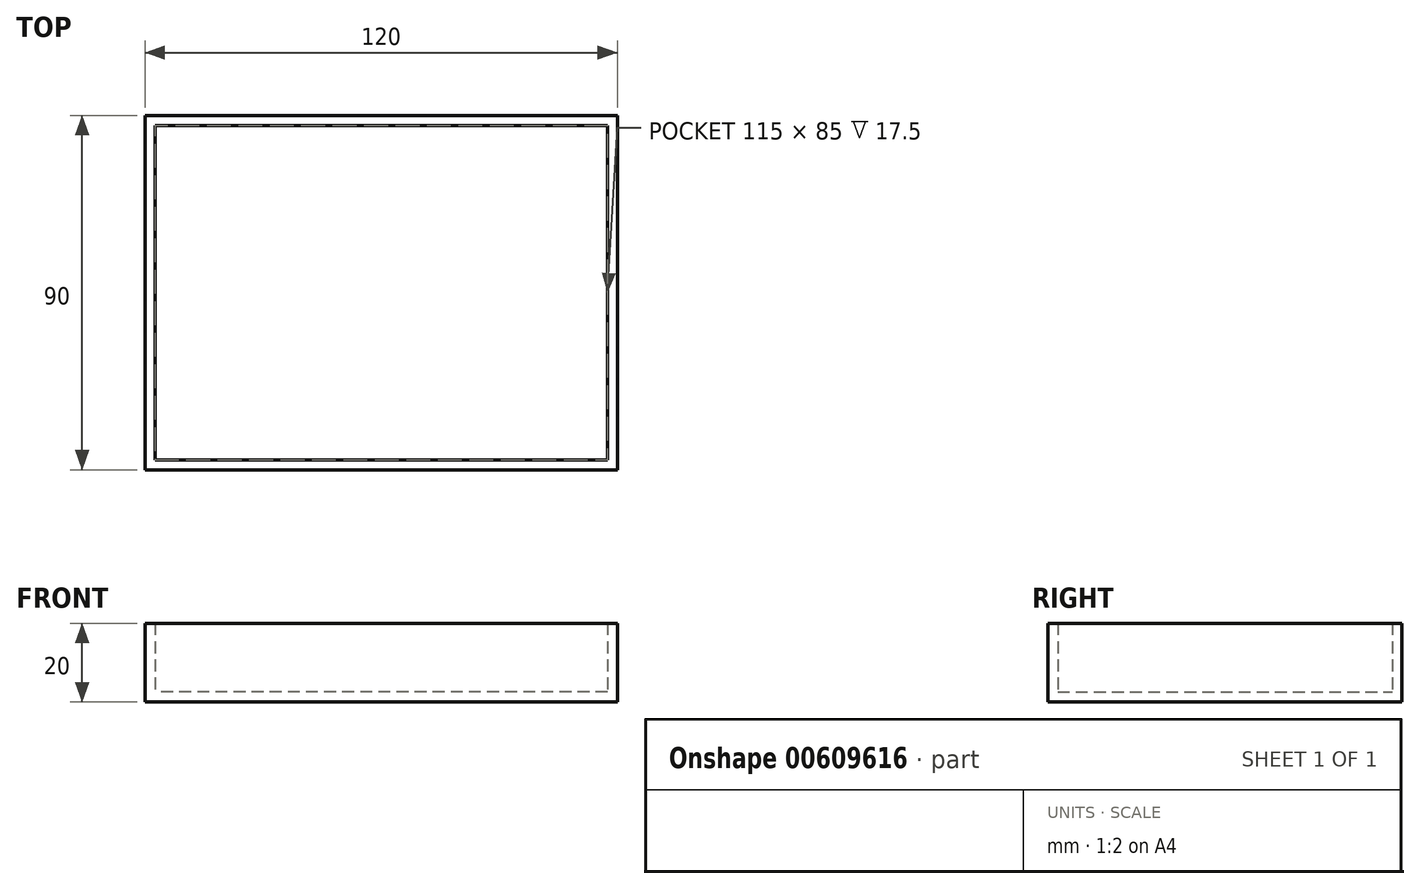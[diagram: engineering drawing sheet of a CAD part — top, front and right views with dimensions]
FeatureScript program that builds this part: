
annotation { "Feature Type Name" : "Feature", "Feature Type Description" : "" }
export const myFeature = defineFeature(function(context is Context, id is Id, definition is map)
    precondition{}
    {
        {
            var Q0;
            Q0=qCreatedBy(makeId("Top.planeOp"),FACE);
            var sketch = newSketch(context, id + "F0", { "sketchPlane" : qUnion([Q0])});
            skLineSegment(sketch, "E0.bottom", {"start": v(60.22, -45.14) * mm, "end": v(-59.78, -45.14) * mm});
            skLineSegment(sketch, "E0.top", {"start": v(60.22, 44.86) * mm, "end": v(-59.78, 44.86) * mm});
            skLineSegment(sketch, "E0.left", {"start": v(60.22, -45.14) * mm, "end": v(60.22, 44.86) * mm});
            skLineSegment(sketch, "E0.right", {"start": v(-59.78, -45.14) * mm, "end": v(-59.78, 44.86) * mm});
            skPoint(sketch, "E0.middle", {"position": v(0.22, -0.14) * mm});
            skSolve(sketch);
        }
        {
            var Q0;
            Q0 = qSketchRegion(id + "F0", true);
            extrude(context, id + "F1", {"entities" : qUnion([Q0]), "depth" : 20 * mm, "offsetDistance" : 25 * mm});
        }
        {
            var Q0;
            Q0=makeQuery(id+"F1.opExtrude","CAP_FACE",FACE,{"disambiguationData":[OSD([sQuery(id+"F0.wireOp",EDGE,"E0.bottom"),sQuery(id+"F0.wireOp",EDGE,"E0.top"),sQuery(id+"F0.wireOp",EDGE,"E0.left"),sQuery(id+"F0.wireOp",EDGE,"E0.right")])],"isStart":false});
            var Q1;
            Q1=makeQuery(id+"F9fx3l9jzPhLckH_1.opFillet","BLEND_FACE",FACE,{"disambiguationData":[OSD([sQuery(id+"F0.wireOp",EDGE,"E0.right")])]});
            shell(context, id + "F2", {"entities" : qUnion([Q0, Q1]), "thickness" : 2.5 * mm});
        }
    });
